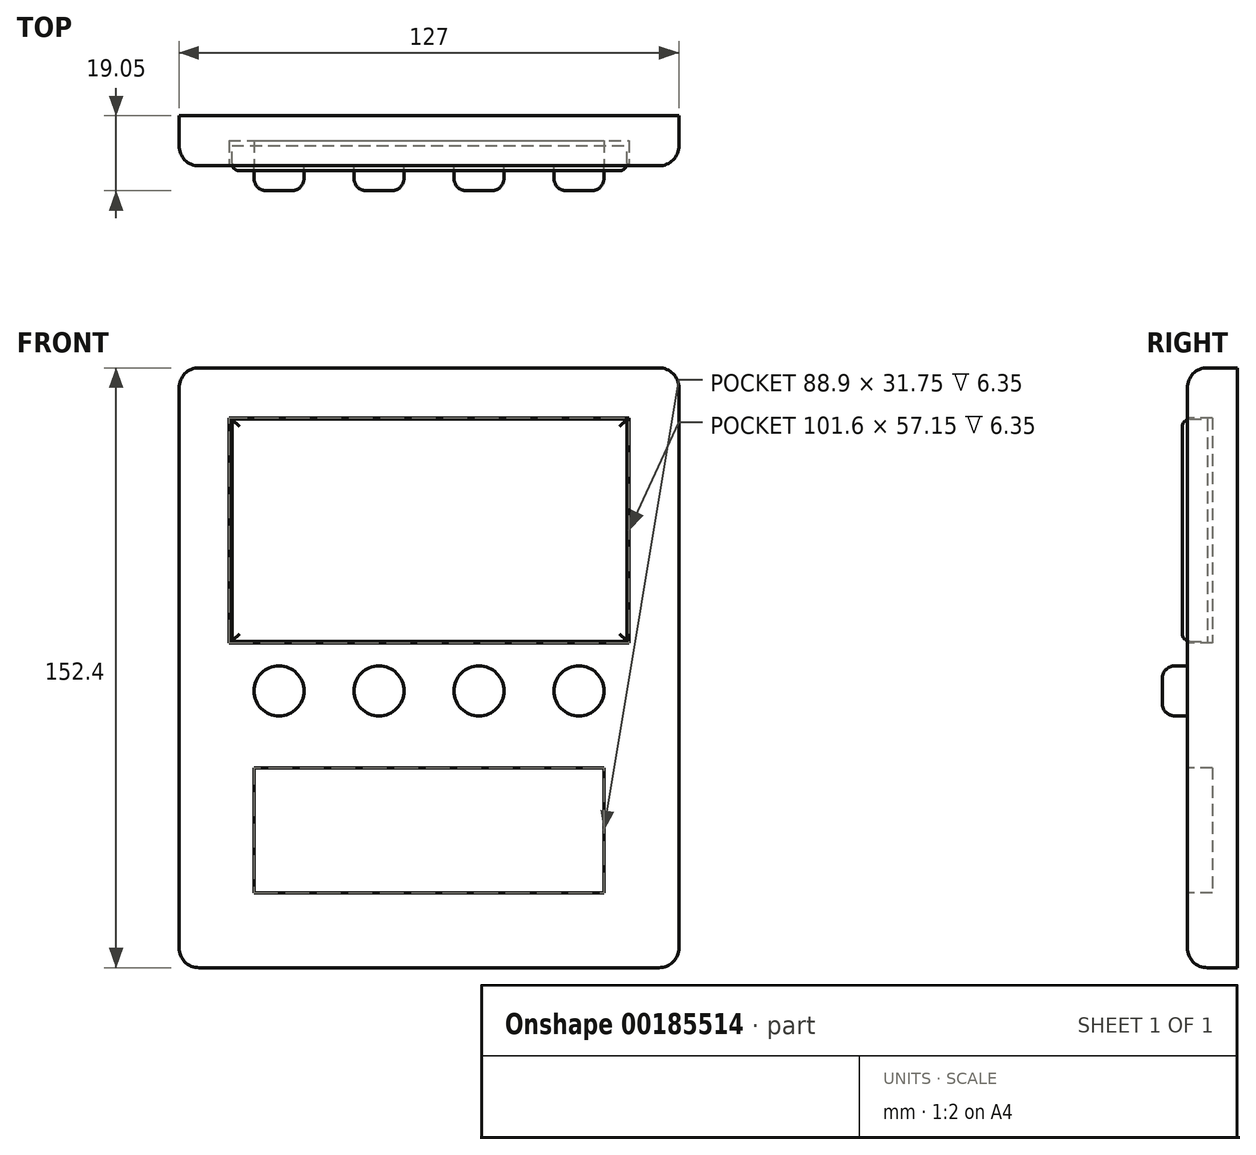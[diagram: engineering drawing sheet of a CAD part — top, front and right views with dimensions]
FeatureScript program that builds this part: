
annotation { "Feature Type Name" : "Feature", "Feature Type Description" : "" }
export const myFeature = defineFeature(function(context is Context, id is Id, definition is map)
    precondition{}
    {
        {
            var Q0;
            Q0=qCreatedBy(makeId("Front.planeOp"),FACE);
            var sketch = newSketch(context, id + "F0", { "sketchPlane" : qUnion([Q0])});
            skLineSegment(sketch, "E0.bottom", {"start": v(63.5, 76.2) * mm, "end": v(-63.5, 76.2) * mm});
            skLineSegment(sketch, "E0.top", {"start": v(63.5, -76.2) * mm, "end": v(-63.5, -76.2) * mm});
            skLineSegment(sketch, "E0.left", {"start": v(63.5, 76.2) * mm, "end": v(63.5, -76.2) * mm});
            skLineSegment(sketch, "E0.right", {"start": v(-63.5, 76.2) * mm, "end": v(-63.5, -76.2) * mm});
            skPoint(sketch, "E0.middle", {"position": v(0, 0) * mm});
            skSolve(sketch);
        }
        {
            var Q0;
            Q0 = qSketchRegion(id + "F0", true);
            extrude(context, id + "F1", {"entities" : qUnion([Q0]), "oppositeDirection" : true, "depth" : 12.7 * mm});
        }
        {
            var Q0;
            Q0=makeQuery(id+"F1.opExtrude","CAP_FACE",FACE,{"disambiguationData":[OSD([sQuery(id+"F0.wireOp",EDGE,"E0.bottom"),sQuery(id+"F0.wireOp",EDGE,"E0.top"),sQuery(id+"F0.wireOp",EDGE,"E0.left"),sQuery(id+"F0.wireOp",EDGE,"E0.right")])],"isStart":true});
            var sketch = newSketch(context, id + "F2", { "sketchPlane" : qUnion([Q0])});
            skLineSegment(sketch, "E1.bottom", {"start": v(-50.8, 63.5) * mm, "end": v(50.8, 63.5) * mm});
            skLineSegment(sketch, "E1.top", {"start": v(-50.8, 6.35) * mm, "end": v(50.8, 6.35) * mm});
            skLineSegment(sketch, "E1.left", {"start": v(-50.8, 63.5) * mm, "end": v(-50.8, 6.35) * mm});
            skLineSegment(sketch, "E1.right", {"start": v(50.8, 63.5) * mm, "end": v(50.8, 6.35) * mm});
            skCircle(sketch, "E2", {"center": v(-38.1, -5.87) * mm, "radius": 6.35 * mm});
            skCircle(sketch, "E3", {"center": v(-12.7, -5.87) * mm, "radius": 6.35 * mm});
            skCircle(sketch, "E4", {"center": v(12.7, -5.87) * mm, "radius": 6.35 * mm});
            skCircle(sketch, "E5", {"center": v(38.1, -5.87) * mm, "radius": 6.35 * mm});
            skLineSegment(sketch, "E6.bottom", {"start": v(-44.45, -25.4) * mm, "end": v(44.45, -25.4) * mm});
            skLineSegment(sketch, "E6.top", {"start": v(-44.45, -57.15) * mm, "end": v(44.45, -57.15) * mm});
            skLineSegment(sketch, "E6.left", {"start": v(-44.45, -25.4) * mm, "end": v(-44.45, -57.15) * mm});
            skLineSegment(sketch, "E6.right", {"start": v(44.45, -25.4) * mm, "end": v(44.45, -57.15) * mm});
            skSolve(sketch);
        }
        {
            var Q0;
            Q0=makeQuery(id+"F2.imprint","IMPRINT",FACE,{"disambiguationData":[TD([[makeQuery(id+"F2.imprint","IMPRINT",EDGE,{"derivedFrom":sQuery(id+"F2.wireOp",EDGE,"E1.bottom")}),-1.0]])]});
            var Q1;
            Q1=makeQuery(id+"F2.imprint","IMPRINT",FACE,{"disambiguationData":[TD([[makeQuery(id+"F2.imprint","IMPRINT",EDGE,{"derivedFrom":sQuery(id+"F2.wireOp",EDGE,"E6.bottom")}),-1.0]])]});
            extrude(context, id + "F3", {"entities" : qUnion([Q0, Q1]), "operationType" : NewBodyOperationType.REMOVE, "oppositeDirection" : true, "depth" : 6.35 * mm});
        }
        {
            var Q0;
            Q0=makeQuery(id+"F2.imprint","IMPRINT",FACE,{"disambiguationData":[TD([[makeQuery(id+"F2.imprint","IMPRINT",EDGE,{"derivedFrom":sQuery(id+"F2.wireOp",EDGE,"E2")}),1.0]])]});
            var Q1;
            Q1=makeQuery(id+"F2.imprint","IMPRINT",FACE,{"disambiguationData":[TD([[makeQuery(id+"F2.imprint","IMPRINT",EDGE,{"derivedFrom":sQuery(id+"F2.wireOp",EDGE,"E3")}),1.0]])]});
            var Q2;
            Q2=makeQuery(id+"F2.imprint","IMPRINT",FACE,{"disambiguationData":[TD([[makeQuery(id+"F2.imprint","IMPRINT",EDGE,{"derivedFrom":sQuery(id+"F2.wireOp",EDGE,"E4")}),1.0]])]});
            var Q3;
            Q3=makeQuery(id+"F2.imprint","IMPRINT",FACE,{"disambiguationData":[TD([[makeQuery(id+"F2.imprint","IMPRINT",EDGE,{"derivedFrom":sQuery(id+"F2.wireOp",EDGE,"E5")}),1.0]])]});
            var Q4;
            Q4=sQuery(id+"F2.wireOp",EDGE,"E2");
            var Q5;
            Q5=sQuery(id+"F2.wireOp",EDGE,"E3");
            var Q6;
            Q6=sQuery(id+"F2.wireOp",EDGE,"E4");
            var Q7;
            Q7=sQuery(id+"F2.wireOp",EDGE,"E5");
            extrude(context, id + "F4", {"entities" : qUnion([Q0, Q1, Q2, Q3]), "surfaceEntities" : qUnion([Q4, Q5, Q6, Q7]), "depth" : 6.35 * mm});
        }
        {
            var Q0;
            Q0=makeQuery(id+"F2.imprint","IMPRINT",FACE,{"disambiguationData":[TD([[makeQuery(id+"F2.imprint","IMPRINT",EDGE,{"derivedFrom":sQuery(id+"F2.wireOp",EDGE,"E1.bottom")}),1.0]])]});
            cPlane(context, id + "F5", {"entities" : qUnion([Q0]), "cplaneType" : CPlaneType.OFFSET, "offset" : 5.08 * mm, "oppositeDirection" : true, "width" : 152.4 * mm, "height" : 152.4 * mm});
        }
        {
            var Q0;
            Q0=qCreatedBy(id+"F5.planeOp",FACE);
            var sketch = newSketch(context, id + "F6", { "sketchPlane" : qUnion([Q0])});
            skLineSegment(sketch, "E7.bottom", {"start": v(-50.05, 63.16) * mm, "end": v(50.3, 63.16) * mm});
            skLineSegment(sketch, "E7.top", {"start": v(-50.05, 6.75) * mm, "end": v(50.3, 6.75) * mm});
            skLineSegment(sketch, "E7.left", {"start": v(-50.05, 63.16) * mm, "end": v(-50.05, 6.75) * mm});
            skLineSegment(sketch, "E7.right", {"start": v(50.3, 63.16) * mm, "end": v(50.3, 6.75) * mm});
            skSolve(sketch);
        }
        {
            var Q0;
            Q0 = qSketchRegion(id + "F6", true);
            extrude(context, id + "F7", {"entities" : qUnion([Q0]), "depth" : 6.35 * mm});
        }
        {
            var Q0;
            Q0=makeQuery(id+"F4.opExtrude","CAP_EDGE",EDGE,{"disambiguationData":[OSD([sQuery(id+"F2.wireOp",EDGE,"E2")])],"isStart":false});
            var Q1;
            Q1=makeQuery(id+"F4.opExtrude","CAP_EDGE",EDGE,{"disambiguationData":[OSD([sQuery(id+"F2.wireOp",EDGE,"E3")])],"isStart":false});
            var Q2;
            Q2=makeQuery(id+"F4.opExtrude","CAP_EDGE",EDGE,{"disambiguationData":[OSD([sQuery(id+"F2.wireOp",EDGE,"E4")])],"isStart":false});
            var Q3;
            Q3=makeQuery(id+"F4.opExtrude","CAP_EDGE",EDGE,{"disambiguationData":[OSD([sQuery(id+"F2.wireOp",EDGE,"E5")])],"isStart":false});
            fillet(context, id + "F8", {"entities" : qUnion([Q0, Q1, Q2, Q3]), "radius" : 3.17 * mm, "tangentPropagation" : true, "allowEdgeOverflow" : false});
        }
        {
            var Q0;
            Q0=makeQuery(id+"F7.opExtrude","CAP_EDGE",EDGE,{"disambiguationData":[OSD([sQuery(id+"F6.wireOp",EDGE,"E7.left")])],"isStart":false});
            var Q1;
            Q1=makeQuery(id+"F7.opExtrude","CAP_EDGE",EDGE,{"disambiguationData":[OSD([sQuery(id+"F6.wireOp",EDGE,"E7.bottom")])],"isStart":false});
            var Q2;
            Q2=makeQuery(id+"F7.opExtrude","CAP_EDGE",EDGE,{"disambiguationData":[OSD([sQuery(id+"F6.wireOp",EDGE,"E7.top")])],"isStart":false});
            var Q3;
            Q3=makeQuery(id+"F7.opExtrude","CAP_EDGE",EDGE,{"disambiguationData":[OSD([sQuery(id+"F6.wireOp",EDGE,"E7.right")])],"isStart":false});
            fillet(context, id + "F9", {"entities" : qUnion([Q0, Q1, Q2, Q3]), "radius" : 1.9 * mm, "tangentPropagation" : true, "allowEdgeOverflow" : false});
        }
        {
            var Q0;
            Q0=makeQuery(id+"F1.opExtrude","SWEPT_EDGE",EDGE,{"disambiguationData":[OSD([sQuery(id+"F0.wireOp",EDGE,"E0.bottom"),sQuery(id+"F0.wireOp",EDGE,"E0.right")])]});
            var Q1;
            Q1=makeQuery(id+"F1.opExtrude","SWEPT_EDGE",EDGE,{"disambiguationData":[OSD([sQuery(id+"F0.wireOp",EDGE,"E0.bottom"),sQuery(id+"F0.wireOp",EDGE,"E0.left")])]});
            var Q2;
            Q2=makeQuery(id+"F1.opExtrude","SWEPT_EDGE",EDGE,{"disambiguationData":[OSD([sQuery(id+"F0.wireOp",EDGE,"E0.top"),sQuery(id+"F0.wireOp",EDGE,"E0.left")])]});
            var Q3;
            Q3=makeQuery(id+"F1.opExtrude","SWEPT_EDGE",EDGE,{"disambiguationData":[OSD([sQuery(id+"F0.wireOp",EDGE,"E0.top"),sQuery(id+"F0.wireOp",EDGE,"E0.right")])]});
            var Q4;
            Q4=makeQuery(id+"F1.opExtrude","CAP_EDGE",EDGE,{"disambiguationData":[OSD([sQuery(id+"F0.wireOp",EDGE,"E0.top")])],"isStart":true});
            var Q5;
            Q5=makeQuery(id+"F1.opExtrude","CAP_EDGE",EDGE,{"disambiguationData":[OSD([sQuery(id+"F0.wireOp",EDGE,"E0.right")])],"isStart":true});
            var Q6;
            Q6=makeQuery(id+"F1.opExtrude","CAP_EDGE",EDGE,{"disambiguationData":[OSD([sQuery(id+"F0.wireOp",EDGE,"E0.left")])],"isStart":true});
            var Q7;
            Q7=makeQuery(id+"F1.opExtrude","CAP_EDGE",EDGE,{"disambiguationData":[OSD([sQuery(id+"F0.wireOp",EDGE,"E0.bottom")])],"isStart":true});
            fillet(context, id + "F10", {"entities" : qUnion([Q0, Q1, Q2, Q3, Q4, Q5, Q6, Q7]), "radius" : 5.08 * mm, "tangentPropagation" : true, "allowEdgeOverflow" : false});
        }
    });
